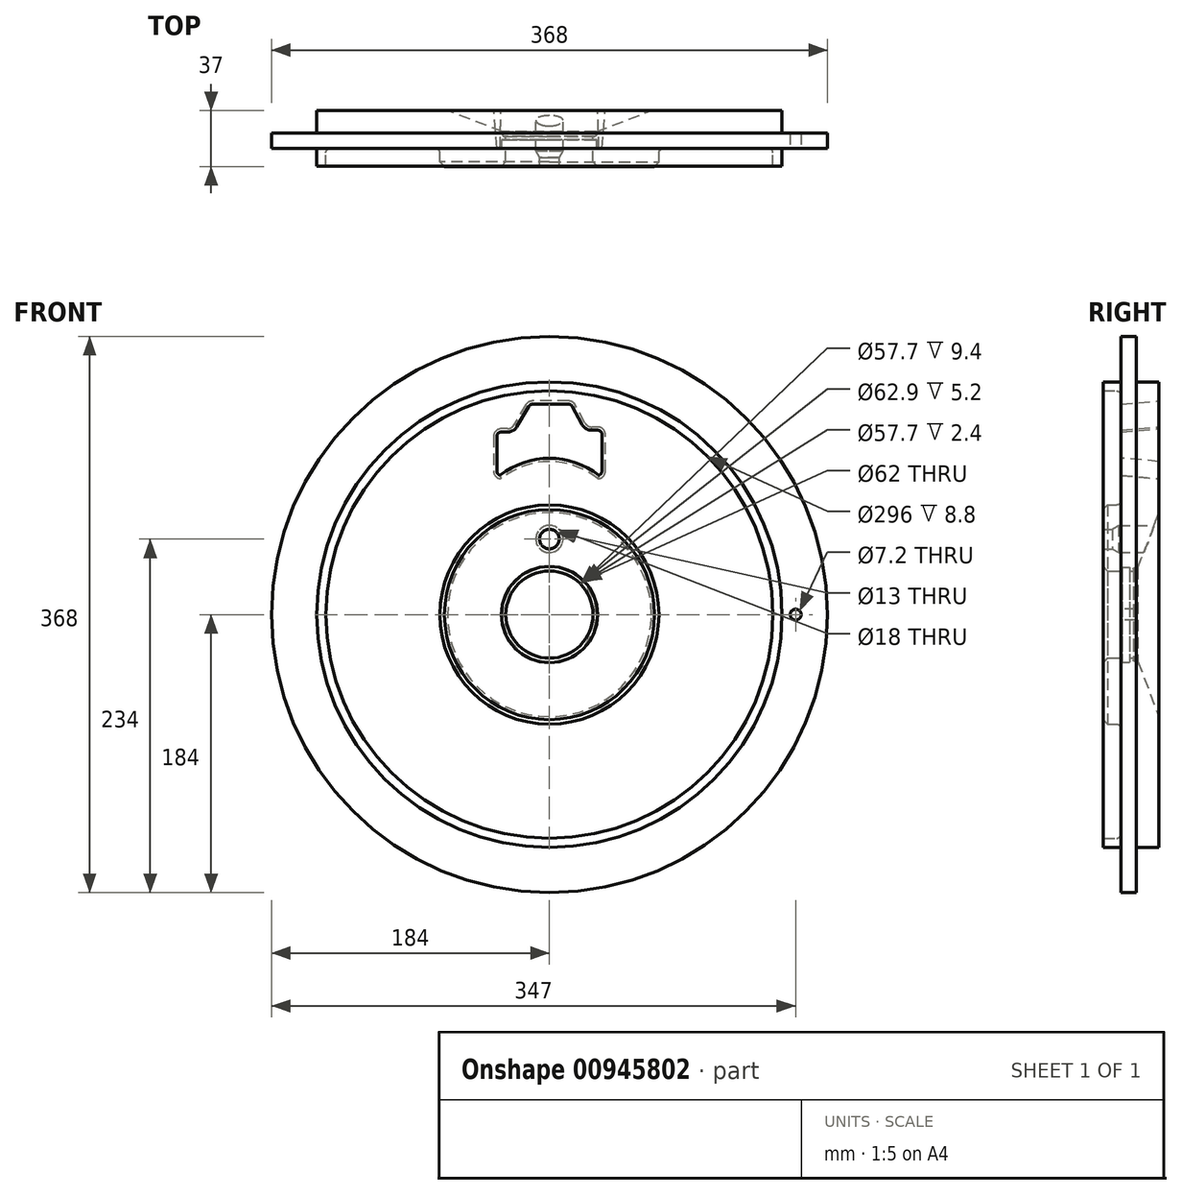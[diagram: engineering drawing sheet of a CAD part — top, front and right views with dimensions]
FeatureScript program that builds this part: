
annotation { "Feature Type Name" : "Feature", "Feature Type Description" : "" }
export const myFeature = defineFeature(function(context is Context, id is Id, definition is map)
    precondition{}
    {
        {
            var Q0;
            Q0=qCreatedBy(makeId("Top.planeOp"),FACE);
            var sketch = newSketch(context, id + "F0", { "sketchPlane" : qUnion([Q0])});
            skLineSegment(sketch, "E0", {"start": v(-72.5, 9) * mm, "end": v(-72.5, 0) * mm});
            skLineSegment(sketch, "E1", {"start": v(-72.5, 0) * mm, "end": v(-28.85, 0) * mm});
            skLineSegment(sketch, "E2", {"start": v(0, 47.35) * mm, "end": v(0, -31.33) * mm, "construction": true});
            skPoint(sketch, "E3.visualSharp", {"position": v(-72.5, 10) * mm});
            skLineSegment(sketch, "E4", {"start": v(-22.07, -0.9) * mm, "end": v(27.18, -0.9) * mm, "construction": true});
            skLineSegment(sketch, "E5", {"start": v(-154, 12) * mm, "end": v(-154, 0.2) * mm});
            skLineSegment(sketch, "E6", {"start": v(-154, 0.2) * mm, "end": v(-148, 0.2) * mm});
            skLineSegment(sketch, "E7", {"start": v(-148, 0.2) * mm, "end": v(-148, 9) * mm});
            skLineSegment(sketch, "E8", {"start": v(-28.85, 20) * mm, "end": v(-30, 20) * mm});
            skPoint(sketch, "E9.visualSharp", {"position": v(-35.7, 20) * mm});
            skLineSegment(sketch, "E10", {"start": v(-28.85, 20) * mm, "end": v(-28.85, 17.6) * mm});
            skLineSegment(sketch, "E11", {"start": v(-28.85, 17.6) * mm, "end": v(-31.45, 17.6) * mm});
            skLineSegment(sketch, "E12", {"start": v(-31.45, 17.6) * mm, "end": v(-31.45, 12.4) * mm});
            skLineSegment(sketch, "E13", {"start": v(-31.45, 12.4) * mm, "end": v(-28.85, 12.4) * mm});
            skLineSegment(sketch, "E14", {"start": v(-28.85, 12.4) * mm, "end": v(-28.85, 0) * mm});
            skLineSegment(sketch, "E15", {"start": v(-154, 12) * mm, "end": v(-184, 12) * mm});
            skLineSegment(sketch, "E16", {"start": v(-154, 37) * mm, "end": v(-67.5, 37) * mm});
            skPoint(sketch, "E17.visualSharp", {"position": v(-35, 23.4) * mm});
            skLineSegment(sketch, "E18", {"start": v(-145, 12) * mm, "end": v(-75.5, 12) * mm});
            skPoint(sketch, "E19.orphan", {"position": v(-148, 11.2) * mm});
            skPoint(sketch, "E20.visualSharp", {"position": v(-148, 12) * mm});
            skArc(sketch, "E20.filletArc", {"start": v(-145, 12) * mm, "mid": v(-147.12, 11.12) * mm, "end": v(-148, 9) * mm});
            skPoint(sketch, "E21.visualSharp", {"position": v(-72.5, 12) * mm});
            skArc(sketch, "E21.filletArc", {"start": v(-72.5, 9) * mm, "mid": v(-73.38, 11.12) * mm, "end": v(-75.5, 12) * mm});
            skLineSegment(sketch, "E22", {"start": v(-184, 12) * mm, "end": v(-184, 22) * mm});
            skLineSegment(sketch, "E23", {"start": v(-184, 22) * mm, "end": v(-154, 22) * mm});
            skLineSegment(sketch, "E24", {"start": v(-154, 22) * mm, "end": v(-154, 37) * mm});
            skLineSegment(sketch, "E25", {"start": v(-31, 23) * mm, "end": v(-67.5, 37) * mm});
            skLineSegment(sketch, "E26", {"start": v(-31, 23) * mm, "end": v(-31, 21) * mm});
            skPoint(sketch, "E27.visualSharp", {"position": v(-31, 20) * mm});
            skArc(sketch, "E27.filletArc", {"start": v(-31, 21) * mm, "mid": v(-30.7, 20.3) * mm, "end": v(-30, 20) * mm});
            skSolve(sketch);
        }
        {
            var Q0;
            Q0=makeQuery(id+"F0.imprint","IMPRINT",FACE,{"disambiguationData":[TD([[makeQuery(id+"F0.imprint","IMPRINT",EDGE,{"derivedFrom":sQuery(id+"F0.wireOp",EDGE,"E0")}),1.0]])]});
            var Q1;
            Q1=sQuery(id+"F0.wireOp",EDGE,"E2");
            revolve(context, id + "F1", {"surfaceOperationType" : NewSurfaceOperationType.NEW, "entities" : qUnion([Q0]), "axis" : qUnion([Q1]), "revolveType" : RevolveType.FULL});
        }
        {
            var Q0;
            Q0=qCreatedBy(makeId("Front.planeOp"),FACE);
            cPlane(context, id + "F2", {"entities" : qUnion([Q0]), "cplaneType" : CPlaneType.OFFSET, "offset" : 38 * mm, "oppositeDirection" : true, "width" : 150 * mm, "height" : 150 * mm});
        }
        {
            var Q0;
            Q0=qCreatedBy(id+"F2.planeOp",FACE);
            var sketch = newSketch(context, id + "F3", { "sketchPlane" : qUnion([Q0])});
            skLineSegment(sketch, "E28", {"start": v(37, 94.82) * mm, "end": v(37, 119.25) * mm});
            skLineSegment(sketch, "E29", {"start": v(32, 124.25) * mm, "end": v(28, 124.25) * mm});
            skLineSegment(sketch, "E30", {"start": v(12.85, 141.42) * mm, "end": v(-11.3, 141.42) * mm});
            skLineSegment(sketch, "E31", {"start": v(-15.6, 138.96) * mm, "end": v(-23.55, 125.5) * mm});
            skLineSegment(sketch, "E32", {"start": v(-27.86, 123.04) * mm, "end": v(-32, 123.04) * mm});
            skLineSegment(sketch, "E33", {"start": v(-37, 118.04) * mm, "end": v(-37, 94.82) * mm});
            skLineSegment(sketch, "E34", {"start": v(0, 22.67) * mm, "end": v(0, 153.69) * mm, "construction": true});
            skLineSegment(sketch, "E35", {"start": v(17.26, 138.77) * mm, "end": v(23.59, 126.9) * mm});
            skPoint(sketch, "E36.visualSharp", {"position": v(15.85, 141.42) * mm});
            skArc(sketch, "E36.filletArc", {"start": v(17.26, 138.77) * mm, "mid": v(15.42, 140.7) * mm, "end": v(12.85, 141.42) * mm});
            skPoint(sketch, "E37.visualSharp", {"position": v(-14.15, 141.42) * mm});
            skArc(sketch, "E37.filletArc", {"start": v(-11.3, 141.42) * mm, "mid": v(-13.78, 140.76) * mm, "end": v(-15.6, 138.96) * mm});
            skPoint(sketch, "E38.visualSharp", {"position": v(-25, 123.04) * mm});
            skArc(sketch, "E38.filletArc", {"start": v(-27.86, 123.04) * mm, "mid": v(-25.38, 123.7) * mm, "end": v(-23.55, 125.5) * mm});
            skPoint(sketch, "E39.visualSharp", {"position": v(-37, 89.82) * mm});
            skArc(sketch, "E39.filletArc", {"start": v(-37, 94.82) * mm, "mid": v(-35.54, 91.28) * mm, "end": v(-32, 89.82) * mm});
            skPoint(sketch, "E40.visualSharp", {"position": v(37, 89.82) * mm});
            skArc(sketch, "E40.filletArc", {"start": v(32, 89.82) * mm, "mid": v(35.54, 91.28) * mm, "end": v(37, 94.82) * mm});
            skPoint(sketch, "E41.visualSharp", {"position": v(37, 124.25) * mm});
            skArc(sketch, "E41.filletArc", {"start": v(37, 119.25) * mm, "mid": v(35.54, 122.78) * mm, "end": v(32, 124.25) * mm});
            skPoint(sketch, "E42.visualSharp", {"position": v(25, 124.25) * mm});
            skArc(sketch, "E42.filletArc", {"start": v(23.59, 126.9) * mm, "mid": v(25.43, 124.96) * mm, "end": v(28, 124.25) * mm});
            skPoint(sketch, "E43.visualSharp", {"position": v(-37, 123.04) * mm});
            skArc(sketch, "E43.filletArc", {"start": v(-32, 123.04) * mm, "mid": v(-35.54, 121.58) * mm, "end": v(-37, 118.04) * mm});
            skArc(sketch, "E44", {"start": v(32, 89.82) * mm, "mid": v(0, 101.22) * mm, "end": v(-32, 89.82) * mm});
            skPoint(sketch, "E44.first.point", {"position": v(0, 0) * mm});
            skSolve(sketch);
        }
        {
            var Q0;
            Q0=qCreatedBy(makeId("Front.planeOp"),FACE);
            var sketch = newSketch(context, id + "F4", { "sketchPlane" : qUnion([Q0])});
            skCircle(sketch, "E45", {"center": v(163, 0) * mm, "radius": 3.6 * mm});
            skSolve(sketch);
        }
        {
            var Q0;
            Q0=qSketchRegion(id+"F4",true);
            extrude(context, id + "F5", {"entities" : qUnion([Q0]), "operationType" : NewBodyOperationType.REMOVE, "oppositeDirection" : true, "depth" : 50 * mm, "offsetDistance" : 25 * mm});
        }
        {
            var Q0;
            Q0=qCreatedBy(makeId("Right.planeOp"),FACE);
            var sketch = newSketch(context, id + "F6", { "sketchPlane" : qUnion([Q0])});
            skLineSegment(sketch, "E46", {"start": v(0, 50) * mm, "end": v(51.06, 50) * mm});
            skLineSegment(sketch, "E47", {"start": v(0, 56.5) * mm, "end": v(6, 56.5) * mm});
            skLineSegment(sketch, "E48", {"start": v(6, 56.5) * mm, "end": v(10.33, 59) * mm});
            skLineSegment(sketch, "E49", {"start": v(10.33, 59) * mm, "end": v(51.06, 59) * mm});
            skLineSegment(sketch, "E50", {"start": v(51.06, 59) * mm, "end": v(51.06, 50) * mm});
            skLineSegment(sketch, "E51", {"start": v(0, 50) * mm, "end": v(0, 56.5) * mm});
            skSolve(sketch);
        }
        {
            var Q0;
            Q0=qSketchRegion(id+"F6",true);
            var Q1;
            Q1=sQuery(id+"F6.wireOp",EDGE,"E46");
            revolve(context, id + "F7", {"operationType" : NewBodyOperationType.REMOVE, "surfaceOperationType" : NewSurfaceOperationType.NEW, "entities" : qUnion([Q0]), "axis" : qUnion([Q1]), "revolveType" : RevolveType.FULL, "oppositeDirection" : true});
        }
        {
            var Q0;
            Q0=makeQuery(id+"F1.opRevolve","SWEPT_EDGE",EDGE,{"disambiguationData":[OSD([sQuery(id+"F0.wireOp",EDGE,"GnCOIqdh-ukie-yiku-SOtR-T2upxGWuMmtm"),sQuery(id+"F0.wireOp",EDGE,"E1")])]});
            chamfer(context, id + "F8", {"entities" : qUnion([Q0]), "width" : 3 * mm, "tangentPropagation" : true});
        }
        {
            var Q0;
            Q0=qSketchRegion(id+"F3",true);
            extrude(context, id + "F9", {"entities" : qUnion([Q0]), "operationType" : NewBodyOperationType.REMOVE, "depth" : 50 * mm, "offsetDistance" : 25 * mm, "hasDraft" : true, "draftAngle" : 5 * degree, "draftPullDirection" : true});
        }
    });
